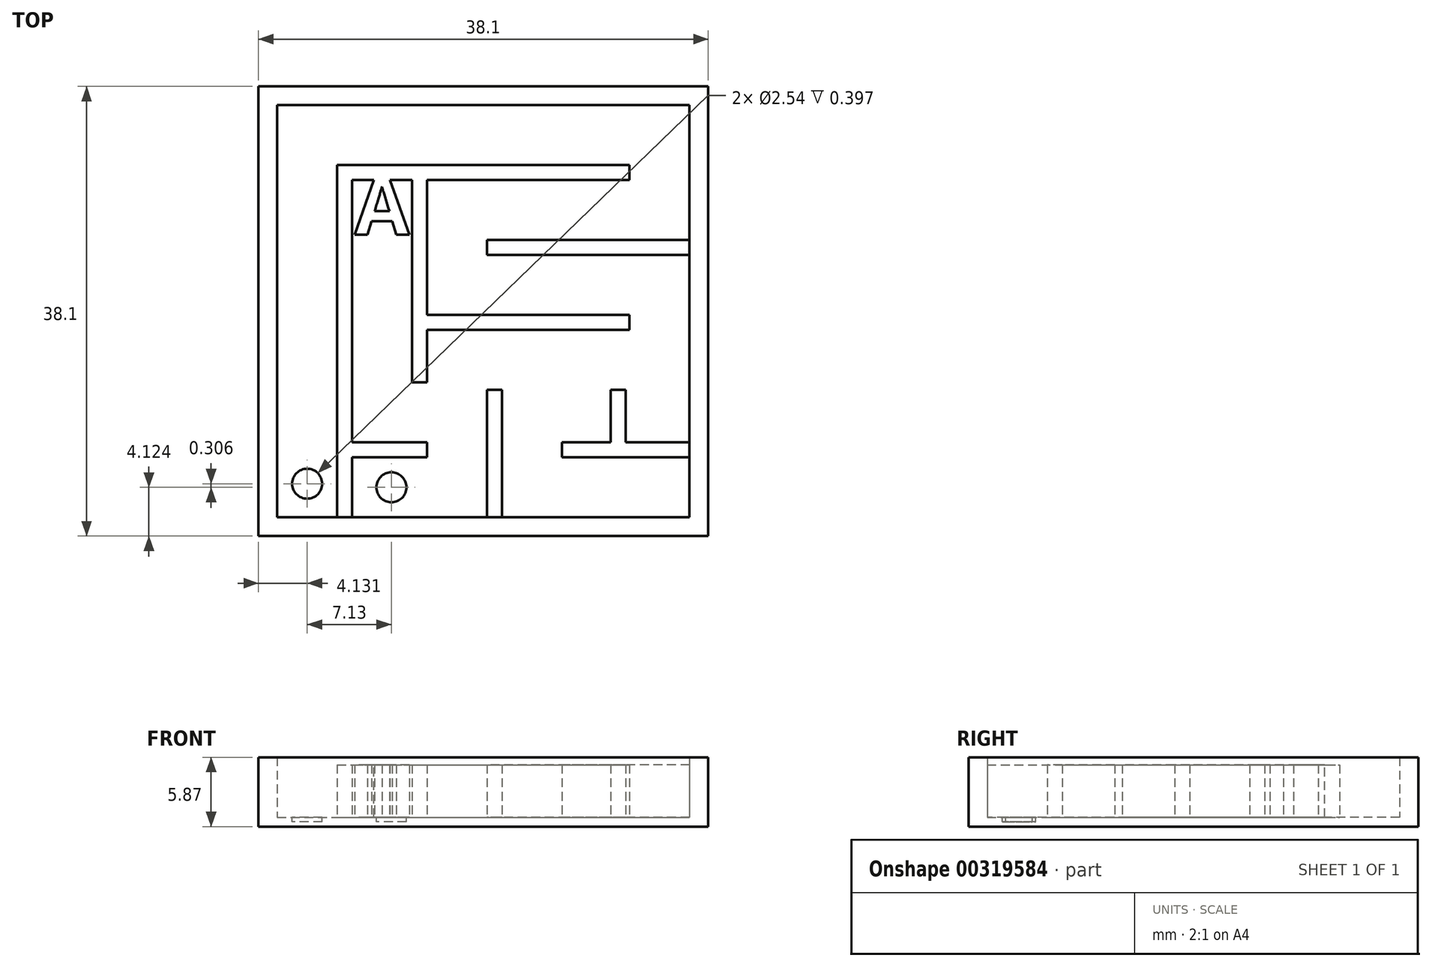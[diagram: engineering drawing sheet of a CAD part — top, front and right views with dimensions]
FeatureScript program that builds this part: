
annotation { "Feature Type Name" : "Feature", "Feature Type Description" : "" }
export const myFeature = defineFeature(function(context is Context, id is Id, definition is map)
    precondition{}
    {
        {
            var Q0;
            Q0=qCreatedBy(makeId("Top.planeOp"),FACE);
            var sketch = newSketch(context, id + "F0", { "sketchPlane" : qUnion([Q0])});
            skLineSegment(sketch, "E0.bottom", {"start": v(-17.97, 32.52) * mm, "end": v(20.13, 32.52) * mm});
            skLineSegment(sketch, "E0.top", {"start": v(-17.97, -5.58) * mm, "end": v(20.13, -5.58) * mm});
            skLineSegment(sketch, "E0.left", {"start": v(-17.97, 32.52) * mm, "end": v(-17.97, -5.58) * mm});
            skLineSegment(sketch, "E0.right", {"start": v(20.13, 32.52) * mm, "end": v(20.13, -5.58) * mm});
            skSolve(sketch);
        }
        {
            var Q0;
            Q0=makeQuery(id+"F0.imprint","IMPRINT",FACE,{"disambiguationData":[TD([[makeQuery(id+"F0.imprint","IMPRINT",EDGE,{"derivedFrom":sQuery(id+"F0.wireOp",EDGE,"E0.bottom")}),-1.0]])]});
            extrude(context, id + "F1", {"entities" : qUnion([Q0]), "depth" : 0.8 * mm});
        }
        {
            var Q0;
            Q0=makeQuery(id+"F1.opExtrude","CAP_FACE",FACE,{"disambiguationData":[OSD([sQuery(id+"F0.wireOp",EDGE,"E0.bottom"),sQuery(id+"F0.wireOp",EDGE,"E0.top"),sQuery(id+"F0.wireOp",EDGE,"E0.left"),sQuery(id+"F0.wireOp",EDGE,"E0.right")])],"isStart":false});
            var sketch = newSketch(context, id + "F2", { "sketchPlane" : qUnion([Q0])});
            skLineSegment(sketch, "E1.0", {"start": v(-16.38, 30.93) * mm, "end": v(18.55, 30.93) * mm});
            skLineSegment(sketch, "E1.1", {"start": v(-16.38, 30.93) * mm, "end": v(-16.38, -4) * mm});
            skLineSegment(sketch, "E1.2", {"start": v(-16.38, -4) * mm, "end": v(18.55, -4) * mm});
            skLineSegment(sketch, "E1.3", {"start": v(18.55, 30.93) * mm, "end": v(18.55, -4) * mm});
            skSolve(sketch);
        }
        {
            var Q0;
            Q0=makeQuery(id+"F2.imprint","IMPRINT",FACE,{"disambiguationData":[TD([[makeQuery(id+"F2.imprint","IMPRINT",EDGE,{"derivedFrom":sQuery(id+"F2.wireOp",EDGE,"E1.0")}),1.0]])]});
            extrude(context, id + "F3", {"entities" : qUnion([Q0]), "operationType" : NewBodyOperationType.ADD, "depth" : 5.08 * mm});
        }
        {
            var Q0;
            Q0=makeQuery(id+"F1.opExtrude","CAP_FACE",FACE,{"disambiguationData":[OSD([sQuery(id+"F0.wireOp",EDGE,"E0.bottom"),sQuery(id+"F0.wireOp",EDGE,"E0.top"),sQuery(id+"F0.wireOp",EDGE,"E0.left"),sQuery(id+"F0.wireOp",EDGE,"E0.right")])],"isStart":false});
            var sketch = newSketch(context, id + "F4", { "sketchPlane" : qUnion([Q0])});
            skLineSegment(sketch, "E2.bottom", {"start": v(-11.3, -4) * mm, "end": v(-10.03, -4) * mm});
            skLineSegment(sketch, "E2.top", {"start": v(-11.3, 25.85) * mm, "end": v(-10.03, 25.85) * mm});
            skLineSegment(sketch, "E2.left", {"start": v(-11.3, -4) * mm, "end": v(-11.3, 25.85) * mm});
            skLineSegment(sketch, "E2.right", {"start": v(-10.03, -4) * mm, "end": v(-10.03, 1.08) * mm});
            skLineSegment(sketch, "E3.bottom", {"start": v(-10.03, 24.58) * mm, "end": v(-4.95, 24.58) * mm});
            skLineSegment(sketch, "E3.top", {"start": v(-10.03, 25.85) * mm, "end": v(13.47, 25.85) * mm});
            skLineSegment(sketch, "E3.right", {"start": v(13.47, 24.58) * mm, "end": v(13.47, 25.85) * mm});
            skLineSegment(sketch, "E4.bottom", {"start": v(-6.22, 24.58) * mm, "end": v(-4.95, 24.58) * mm});
            skLineSegment(sketch, "E4.right", {"start": v(-3.68, 24.58) * mm, "end": v(-3.68, 13.27) * mm});
            skLineSegment(sketch, "E5.top", {"start": v(-4.95, 7.43) * mm, "end": v(-3.68, 7.43) * mm});
            skLineSegment(sketch, "E5.left", {"start": v(-4.95, 13.27) * mm, "end": v(-4.95, 7.43) * mm});
            skLineSegment(sketch, "E5.right", {"start": v(-3.68, 13.27) * mm, "end": v(-3.68, 13.15) * mm});
            skLineSegment(sketch, "E6.bottom", {"start": v(-3.68, 13.15) * mm, "end": v(13.47, 13.15) * mm});
            skLineSegment(sketch, "E6.top", {"start": v(-3.68, 11.88) * mm, "end": v(13.47, 11.88) * mm});
            skLineSegment(sketch, "E6.right", {"start": v(13.47, 13.15) * mm, "end": v(13.47, 11.88) * mm});
            skLineSegment(sketch, "E7.bottom", {"start": v(18.55, 19.5) * mm, "end": v(1.4, 19.5) * mm});
            skLineSegment(sketch, "E7.top", {"start": v(18.55, 18.23) * mm, "end": v(1.4, 18.23) * mm});
            skLineSegment(sketch, "E7.left", {"start": v(18.55, 19.5) * mm, "end": v(18.55, 18.23) * mm});
            skLineSegment(sketch, "E7.right", {"start": v(1.4, 19.5) * mm, "end": v(1.4, 18.23) * mm});
            skLineSegment(sketch, "E8.bottom", {"start": v(2.67, -4) * mm, "end": v(1.4, -4) * mm});
            skLineSegment(sketch, "E8.top", {"start": v(2.67, 6.8) * mm, "end": v(1.4, 6.8) * mm});
            skLineSegment(sketch, "E8.left", {"start": v(2.67, -4) * mm, "end": v(2.67, 6.8) * mm});
            skLineSegment(sketch, "E8.right", {"start": v(1.4, -4) * mm, "end": v(1.4, 6.8) * mm});
            skLineSegment(sketch, "E9.bottom", {"start": v(-10.03, 1.08) * mm, "end": v(-3.68, 1.08) * mm});
            skLineSegment(sketch, "E9.top", {"start": v(-10.03, 2.35) * mm, "end": v(-3.68, 2.35) * mm});
            skLineSegment(sketch, "E9.right", {"start": v(-3.68, 1.08) * mm, "end": v(-3.68, 2.35) * mm});
            skLineSegment(sketch, "E10.trimOffspring", {"start": v(-3.68, 13.27) * mm, "end": v(-3.68, 13.27) * mm});
            skLineSegment(sketch, "E11.trimOffspring", {"start": v(-10.03, 25.85) * mm, "end": v(-10.03, 25.85) * mm});
            skLineSegment(sketch, "E12", {"start": v(-4.95, 13.27) * mm, "end": v(-4.95, 24.58) * mm});
            skLineSegment(sketch, "E13.bottom", {"start": v(18.55, 2.35) * mm, "end": v(13.15, 2.35) * mm});
            skLineSegment(sketch, "E13.top", {"start": v(18.55, 1.08) * mm, "end": v(7.75, 1.08) * mm});
            skLineSegment(sketch, "E13.left", {"start": v(18.55, 2.35) * mm, "end": v(18.55, 1.08) * mm});
            skLineSegment(sketch, "E13.right", {"start": v(7.75, 2.35) * mm, "end": v(7.75, 1.08) * mm});
            skLineSegment(sketch, "E14.trimOffspring", {"start": v(-3.68, 24.58) * mm, "end": v(13.47, 24.58) * mm});
            skLineSegment(sketch, "E15.trimOffspring", {"start": v(-3.68, 11.88) * mm, "end": v(-3.68, 7.43) * mm});
            skLineSegment(sketch, "E16.top", {"start": v(13.15, 6.8) * mm, "end": v(11.88, 6.8) * mm});
            skLineSegment(sketch, "E16.right", {"start": v(11.88, 2.35) * mm, "end": v(11.88, 6.8) * mm});
            skLineSegment(sketch, "E17.trimOffspring", {"start": v(11.88, 2.35) * mm, "end": v(7.75, 2.35) * mm});
            skLineSegment(sketch, "E18", {"start": v(13.15, 6.8) * mm, "end": v(13.15, 2.35) * mm});
            skLineSegment(sketch, "E19.trimOffspring", {"start": v(-10.03, 2.35) * mm, "end": v(-10.03, 24.58) * mm});
            skLineSegment(sketch, "E20", {"start": v(-16.38, -4) * mm, "end": v(-11.3, -4) * mm});
            skPoint(sketch, "E21.centerSnap0", {"position": v(-13.84, -4) * mm});
            skCircle(sketch, "E22", {"center": v(-13.84, -1.15) * mm, "radius": 1.27 * mm});
            skLineSegment(sketch, "E23", {"start": v(-10.03, 1.08) * mm, "end": v(-10.03, -4) * mm});
            skCircle(sketch, "E24", {"center": v(-6.7, -1.46) * mm, "radius": 1.27 * mm});
            skPoint(sketch, "E24.centerSnap0", {"position": v(-10.03, -1.46) * mm});
            skSolve(sketch);
        }
        {
            var Q0;
            Q0=makeQuery(id+"F4.imprint","IMPRINT",FACE,{"disambiguationData":[TD([[makeQuery(id+"F4.imprint","IMPRINT",EDGE,{"derivedFrom":sQuery(id+"F4.wireOp",EDGE,"E22")}),1.0]])]});
            var Q1;
            Q1=makeQuery(id+"F4.imprint","IMPRINT",FACE,{"disambiguationData":[TD([[makeQuery(id+"F4.imprint","IMPRINT",EDGE,{"derivedFrom":sQuery(id+"F4.wireOp",EDGE,"E24")}),1.0]])]});
            extrude(context, id + "F5", {"entities" : qUnion([Q0, Q1]), "operationType" : NewBodyOperationType.REMOVE, "oppositeDirection" : true, "depth" : 0.4 * mm});
        }
        {
            var Q0;
            Q0=makeQuery(id+"F4.imprint","IMPRINT",FACE,{"disambiguationData":[TD([[makeQuery(id+"F4.imprint","IMPRINT",EDGE,{"derivedFrom":sQuery(id+"F4.wireOp",EDGE,"E2.bottom")}),1.0]])]});
            var Q1;
            Q1=makeQuery(id+"F4.imprint","IMPRINT",FACE,{"disambiguationData":[TD([[makeQuery(id+"F4.imprint","IMPRINT",EDGE,{"derivedFrom":sQuery(id+"F4.wireOp",EDGE,"E8.bottom")}),1.0]])]});
            var Q2;
            Q2=makeQuery(id+"F4.imprint","IMPRINT",FACE,{"disambiguationData":[TD([[makeQuery(id+"F4.imprint","IMPRINT",EDGE,{"derivedFrom":sQuery(id+"F4.wireOp",EDGE,"E13.bottom")}),1.0]])]});
            var Q3;
            Q3=makeQuery(id+"F4.imprint","IMPRINT",FACE,{"disambiguationData":[TD([[makeQuery(id+"F4.imprint","IMPRINT",EDGE,{"derivedFrom":sQuery(id+"F4.wireOp",EDGE,"E7.bottom")}),1.0]])]});
            extrude(context, id + "F6", {"entities" : qUnion([Q0, Q1, Q2, Q3]), "operationType" : NewBodyOperationType.ADD, "depth" : 4.44 * mm});
        }
        {
            var Q0;
            Q0=makeQuery(id+"F4.imprint","IMPRINT",FACE,{"disambiguationData":[TD([[makeQuery(id+"F4.imprint","IMPRINT",EDGE,{"derivedFrom":sQuery(id+"F4.wireOp",EDGE,"E2.top")}),1.0]])]});
            var sketch = newSketch(context, id + "F7", { "sketchPlane" : qUnion([Q0])});
            skText(sketch, "E25", { "text": "A", "fontName": "OpenSans-Bold.ttf"});
            const initialGuessF7  = {"E25": [-0.00983, 0.01995, 1, 0, 0.00485]};
            skSetInitialGuess(sketch, initialGuessF7);
            skSolve(sketch);
        }
        {
            var Q0;
            Q0 = qSketchRegion(id + "F7", true);
            extrude(context, id + "F8", {"entities" : qUnion([Q0]), "operationType" : NewBodyOperationType.ADD, "depth" : 4.44 * mm});
        }
    });
